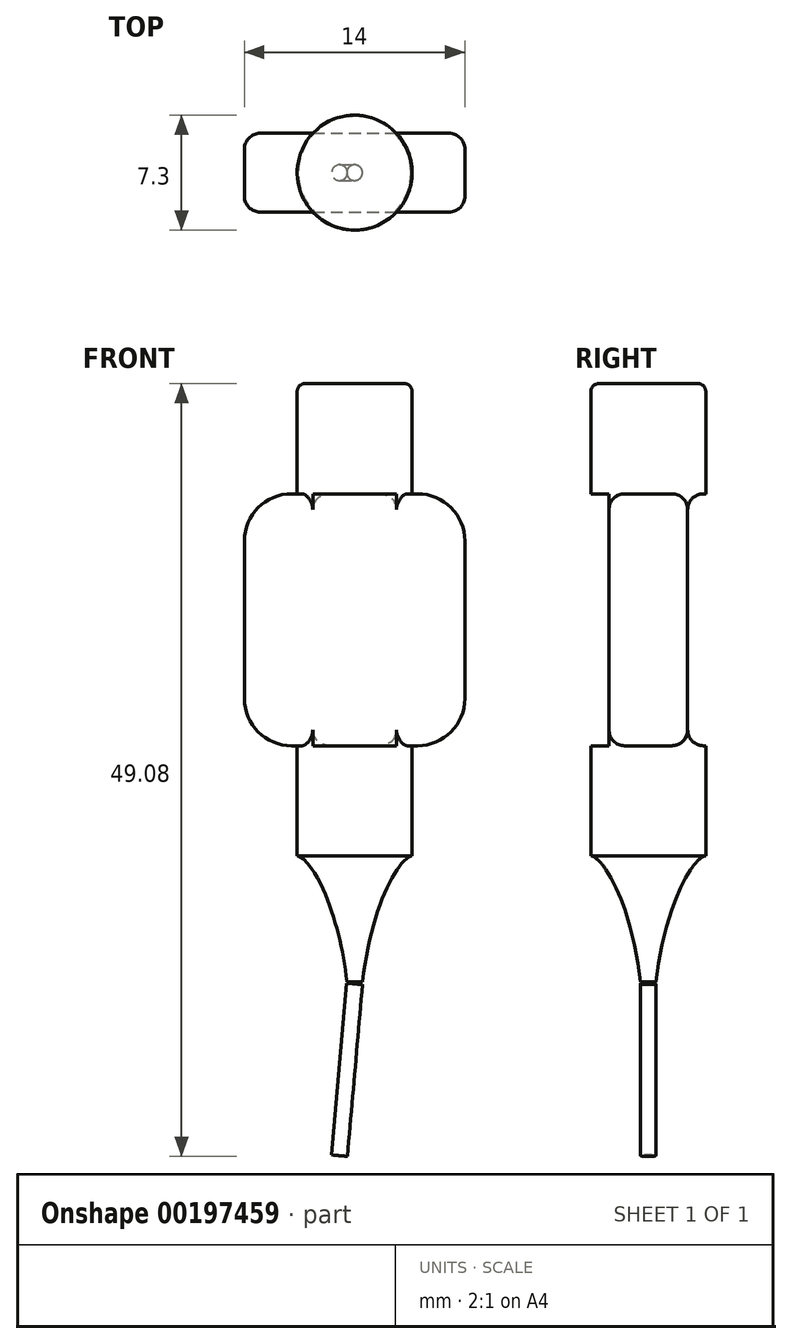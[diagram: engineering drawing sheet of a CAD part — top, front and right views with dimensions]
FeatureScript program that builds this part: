
annotation { "Feature Type Name" : "Feature", "Feature Type Description" : "" }
export const myFeature = defineFeature(function(context is Context, id is Id, definition is map)
    precondition{}
    {
        {
            var Q0;
            Q0=qCreatedBy(makeId("Top.planeOp"),FACE);
            var sketch = newSketch(context, id + "F0", { "sketchPlane" : qUnion([Q0])});
            skCircle(sketch, "E0", {"center": v(0, 0) * mm, "radius": 3.65 * mm});
            skSolve(sketch);
        }
        {
            var Q0;
            Q0=makeQuery(id+"F0.imprint","IMPRINT",FACE,{"disambiguationData":[TD([[makeQuery(id+"F0.imprint","IMPRINT",EDGE,{"derivedFrom":sQuery(id+"F0.wireOp",EDGE,"E0")}),1.0]])]});
            extrude(context, id + "F1", {"entities" : qUnion([Q0]), "depth" : 30 * mm});
        }
        {
            var Q0;
            Q0=qCreatedBy(makeId("Front.planeOp"),FACE);
            var sketch = newSketch(context, id + "F2", { "sketchPlane" : qUnion([Q0])});
            skLineSegment(sketch, "E1.bottom", {"start": v(-7, 23) * mm, "end": v(7, 23) * mm});
            skLineSegment(sketch, "E1.top", {"start": v(-7, 7) * mm, "end": v(7, 7) * mm});
            skLineSegment(sketch, "E1.left", {"start": v(-7, 23) * mm, "end": v(-7, 7) * mm});
            skLineSegment(sketch, "E1.right", {"start": v(7, 23) * mm, "end": v(7, 7) * mm});
            skSolve(sketch);
        }
        {
            var Q0;
            Q0=makeQuery(id+"F2.imprint","IMPRINT",FACE,{"disambiguationData":[TD([[makeQuery(id+"F2.imprint","IMPRINT",EDGE,{"derivedFrom":sQuery(id+"F2.wireOp",EDGE,"E1.bottom")}),-1.0]])]});
            extrude(context, id + "F3", {"entities" : qUnion([Q0]), "endBound" : BoundingType.SYMMETRIC, "depth" : 10 * mm});
        }
        {
            var Q0;
            Q0=makeQuery(id+"F3.opExtrude","SWEPT_BODY",BODY,{"disambiguationData":[OSD([sQuery(id+"F2.wireOp",EDGE,"E1.bottom"),sQuery(id+"F2.wireOp",EDGE,"E1.top"),sQuery(id+"F2.wireOp",EDGE,"E1.left"),sQuery(id+"F2.wireOp",EDGE,"E1.right")])]});
            var Q1;
            Q1=makeQuery(id+"F1.opExtrude","SWEPT_BODY",BODY,{"disambiguationData":[OSD([sQuery(id+"F0.wireOp",EDGE,"E0")])]});
            booleanBodies(context, id + "F4", {"operationType" : BooleanOperationType.SUBTRACTION, "tools" : qUnion([Q0]), "targets" : qUnion([Q1])});
        }
        {
            var Q0;
            Q0 = qSketchRegion(id + "F2", true);
            extrude(context, id + "F5", {"entities" : qUnion([Q0]), "operationType" : NewBodyOperationType.ADD, "endBound" : BoundingType.SYMMETRIC, "depth" : 5 * mm});
        }
        {
            var Q0;
            Q0=makeQuery(id+"F5.opExtrude","SWEPT_EDGE",EDGE,{"disambiguationData":[OSD([sQuery(id+"F2.wireOp",EDGE,"E1.bottom"),sQuery(id+"F2.wireOp",EDGE,"E1.right")])]});
            var Q1;
            Q1=makeQuery(id+"F5.opExtrude","SWEPT_EDGE",EDGE,{"disambiguationData":[OSD([sQuery(id+"F2.wireOp",EDGE,"E1.top"),sQuery(id+"F2.wireOp",EDGE,"E1.right")])]});
            var Q2;
            Q2=makeQuery(id+"F5.opExtrude","SWEPT_EDGE",EDGE,{"disambiguationData":[OSD([sQuery(id+"F2.wireOp",EDGE,"E1.bottom"),sQuery(id+"F2.wireOp",EDGE,"E1.left")])]});
            var Q3;
            Q3=makeQuery(id+"F5.opExtrude","SWEPT_EDGE",EDGE,{"disambiguationData":[OSD([sQuery(id+"F2.wireOp",EDGE,"E1.top"),sQuery(id+"F2.wireOp",EDGE,"E1.left")])]});
            fillet(context, id + "F6", {"entities" : qUnion([Q0, Q1, Q2, Q3]), "radius" : 3 * mm, "tangentPropagation" : true, "allowEdgeOverflow" : false});
        }
        {
            var Q0;
            Q0=makeQuery(id+"F5.opExtrude","CAP_EDGE",EDGE,{"disambiguationData":[OSD([sQuery(id+"F2.wireOp",EDGE,"E1.left")])],"isStart":false});
            var Q1;
            Q1=makeQuery(id+"F5.opExtrude","CAP_EDGE",EDGE,{"disambiguationData":[OSD([sQuery(id+"F2.wireOp",EDGE,"E1.right")])],"isStart":false});
            var Q2;
            Q2=makeQuery(id+"F5.opExtrude","CAP_EDGE",EDGE,{"disambiguationData":[OSD([sQuery(id+"F2.wireOp",EDGE,"E1.left")])],"isStart":true});
            var Q3;
            Q3=makeQuery(id+"F5.opExtrude","CAP_EDGE",EDGE,{"disambiguationData":[OSD([sQuery(id+"F2.wireOp",EDGE,"E1.right")])],"isStart":true});
            fillet(context, id + "F7", {"entities" : qUnion([Q0, Q1, Q2, Q3]), "radius" : 1 * mm, "tangentPropagation" : true, "allowEdgeOverflow" : false});
        }
        {
            var Q0;
            {var subQ0=sQuery(id+"F2.wireOp",EDGE,"E1.bottom");Q0=makeQuery(id+"F5.boolean.opBoolean","SPLIT",EDGE,{"disambiguationData":[topologyDisambiguationEdgeConnected([makeQuery(id+"F4.opBoolean","COPY",FACE,{"derivedFrom":makeQuery(id+"F3.opExtrude","SWEPT_FACE",FACE,{"disambiguationData":[OSD([subQ0])]})}),makeQuery(id+"F5.opExtrude","CAP_FACE",FACE,{"disambiguationData":[OSD([subQ0,sQuery(id+"F2.wireOp",EDGE,"E1.top"),sQuery(id+"F2.wireOp",EDGE,"E1.left"),sQuery(id+"F2.wireOp",EDGE,"E1.right")])],"isStart":true})])],"derivedFrom":makeQuery(id+"F5.opExtrude","CAP_EDGE",EDGE,{"disambiguationData":[OSD([subQ0])],"isStart":true})});}
            var Q1;
            {var subQ0=sQuery(id+"F2.wireOp",EDGE,"E1.top");Q1=makeQuery(id+"F5.boolean.opBoolean","SPLIT",EDGE,{"disambiguationData":[topologyDisambiguationEdgeConnected([makeQuery(id+"F4.opBoolean","COPY",FACE,{"derivedFrom":makeQuery(id+"F3.opExtrude","SWEPT_FACE",FACE,{"disambiguationData":[OSD([subQ0])]})}),makeQuery(id+"F5.opExtrude","CAP_FACE",FACE,{"disambiguationData":[OSD([sQuery(id+"F2.wireOp",EDGE,"E1.bottom"),subQ0,sQuery(id+"F2.wireOp",EDGE,"E1.left"),sQuery(id+"F2.wireOp",EDGE,"E1.right")])],"isStart":true})])],"derivedFrom":makeQuery(id+"F5.opExtrude","CAP_EDGE",EDGE,{"disambiguationData":[OSD([subQ0])],"isStart":true})});}
            var Q2;
            {var subQ0=sQuery(id+"F2.wireOp",EDGE,"E1.top");Q2=makeQuery(id+"F5.boolean.opBoolean","SPLIT",EDGE,{"disambiguationData":[topologyDisambiguationEdgeConnected([makeQuery(id+"F4.opBoolean","COPY",FACE,{"derivedFrom":makeQuery(id+"F3.opExtrude","SWEPT_FACE",FACE,{"disambiguationData":[OSD([subQ0])]})}),makeQuery(id+"F5.opExtrude","CAP_FACE",FACE,{"disambiguationData":[OSD([sQuery(id+"F2.wireOp",EDGE,"E1.bottom"),subQ0,sQuery(id+"F2.wireOp",EDGE,"E1.left"),sQuery(id+"F2.wireOp",EDGE,"E1.right")])],"isStart":false})])],"derivedFrom":makeQuery(id+"F5.opExtrude","CAP_EDGE",EDGE,{"disambiguationData":[OSD([subQ0])],"isStart":false})});}
            var Q3;
            {var subQ0=sQuery(id+"F2.wireOp",EDGE,"E1.bottom");Q3=makeQuery(id+"F5.boolean.opBoolean","SPLIT",EDGE,{"disambiguationData":[topologyDisambiguationEdgeConnected([makeQuery(id+"F4.opBoolean","COPY",FACE,{"derivedFrom":makeQuery(id+"F3.opExtrude","SWEPT_FACE",FACE,{"disambiguationData":[OSD([subQ0])]})}),makeQuery(id+"F5.opExtrude","CAP_FACE",FACE,{"disambiguationData":[OSD([subQ0,sQuery(id+"F2.wireOp",EDGE,"E1.top"),sQuery(id+"F2.wireOp",EDGE,"E1.left"),sQuery(id+"F2.wireOp",EDGE,"E1.right")])],"isStart":false})])],"derivedFrom":makeQuery(id+"F5.opExtrude","CAP_EDGE",EDGE,{"disambiguationData":[OSD([subQ0])],"isStart":false})});}
            fillet(context, id + "F8", {"entities" : qUnion([Q0, Q1, Q2, Q3]), "radius" : 1 * mm, "tangentPropagation" : true, "allowEdgeOverflow" : false});
        }
        {
            var Q0;
            Q0=makeQuery(id+"F1.opExtrude","CAP_EDGE",EDGE,{"disambiguationData":[OSD([sQuery(id+"F0.wireOp",EDGE,"E0")])],"isStart":false});
            fillet(context, id + "F9", {"entities" : qUnion([Q0]), "radius" : 0.5 * mm, "tangentPropagation" : true, "allowEdgeOverflow" : false});
        }
        {
            var Q0;
            Q0=qCreatedBy(makeId("Front.planeOp"),FACE);
            var sketch = newSketch(context, id + "F10", { "sketchPlane" : qUnion([Q0])});
            skLineSegment(sketch, "E2", {"start": v(3.58, 0) * mm, "end": v(0, 0) * mm, "construction": true});
            skSolve(sketch);
        }
        {
            var Q0;
            Q0=qCreatedBy(makeId("Front.planeOp"),FACE);
            var sketch = newSketch(context, id + "F11", { "sketchPlane" : qUnion([Q0])});
            skLineSegment(sketch, "E3", {"start": v(0, 2.52) * mm, "end": v(0, -8) * mm, "construction": true});
            skLineSegment(sketch, "E4", {"start": v(0, -8) * mm, "end": v(0.5, -8) * mm});
            skFitSpline(sketch, "E5", {"points": [v(0.5, -8) * mm, v(3.58, 0) * mm], "startDerivative": vector(1.42, 12.94) * mm, "endDerivative": vector(3.16, 1.32) * mm});
            skLineSegment(sketch, "E6", {"start": v(3.58, 0) * mm, "end": v(0, 0) * mm});
            skLineSegment(sketch, "E7", {"start": v(0, 0) * mm, "end": v(0, -8) * mm});
            skSolve(sketch);
        }
        {
            var Q0;
            Q0=makeQuery(id+"F11.imprint","IMPRINT",FACE,{"disambiguationData":[TD([[makeQuery(id+"F11.imprint","IMPRINT",EDGE,{"derivedFrom":sQuery(id+"F11.wireOp",EDGE,"E4")}),1.0]])]});
            var Q1;
            Q1=sQuery(id+"F11.wireOp",EDGE,"E7");
            revolve(context, id + "F12", {"operationType" : NewBodyOperationType.ADD, "entities" : qUnion([Q0]), "axis" : qUnion([Q1]), "revolveType" : RevolveType.FULL});
        }
        {
            var Q0;
            Q0=qCreatedBy(makeId("Front.planeOp"),FACE);
            var sketch = newSketch(context, id + "F13", { "sketchPlane" : qUnion([Q0])});
            skLineSegment(sketch, "E8", {"start": v(0, -8.08) * mm, "end": v(-0.96, -19.04) * mm});
            skLineSegment(sketch, "E9", {"start": v(-0.96, -19.04) * mm, "end": v(-1.46, -19) * mm});
            skLineSegment(sketch, "E10", {"start": v(-1.46, -19) * mm, "end": v(-0.5, -8.08) * mm});
            skLineSegment(sketch, "E11", {"start": v(-0.5, -8.08) * mm, "end": v(0, -8.08) * mm});
            skSolve(sketch);
        }
        {
            var Q0;
            Q0=makeQuery(id+"F13.imprint","IMPRINT",FACE,{"disambiguationData":[TD([[makeQuery(id+"F13.imprint","IMPRINT",EDGE,{"derivedFrom":sQuery(id+"F13.wireOp",EDGE,"E8")}),-1.0]])]});
            var Q1;
            Q1=sQuery(id+"F13.wireOp",EDGE,"E8");
            revolve(context, id + "F14", {"entities" : qUnion([Q0]), "axis" : qUnion([Q1]), "revolveType" : RevolveType.FULL});
        }
    });
